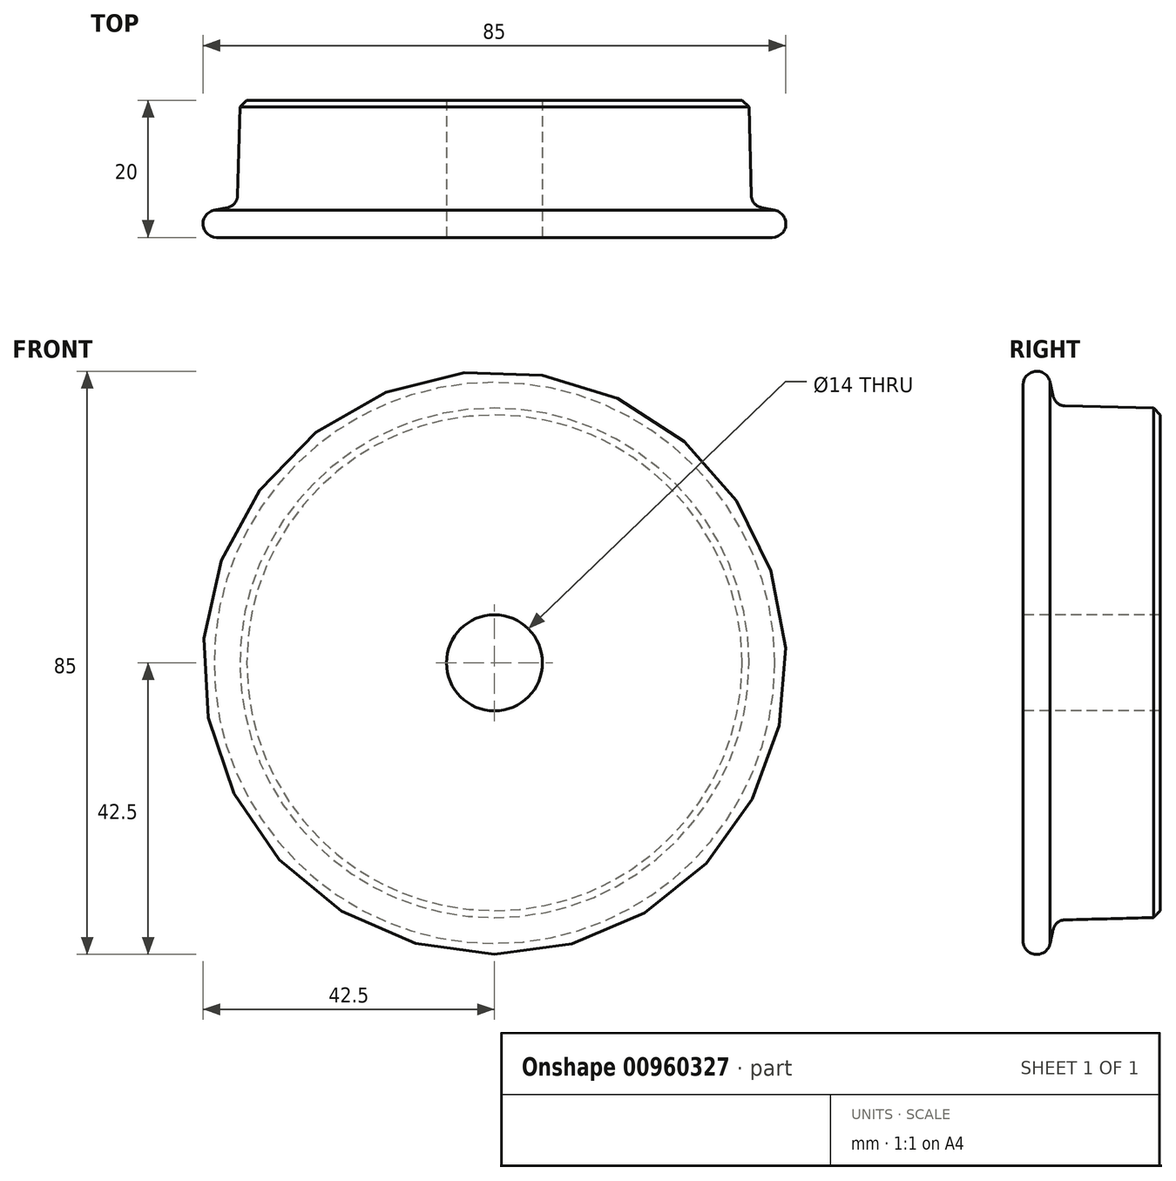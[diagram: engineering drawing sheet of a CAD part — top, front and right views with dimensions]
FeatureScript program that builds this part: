
annotation { "Feature Type Name" : "Feature", "Feature Type Description" : "" }
export const myFeature = defineFeature(function(context is Context, id is Id, definition is map)
    precondition{}
    {
        {
            var Q0;
            Q0=qCreatedBy(makeId("Right.planeOp"),FACE);
            var sketch = newSketch(context, id + "F0", { "sketchPlane" : qUnion([Q0])});
            skLineSegment(sketch, "E0", {"start": v(-29.18, 0) * mm, "end": v(26, 0) * mm, "construction": true});
            skLineSegment(sketch, "E1", {"start": v(0, 0) * mm, "end": v(0, 48.26) * mm, "construction": true});
            skLineSegment(sketch, "E2.0", {"start": v(-10, 7) * mm, "end": v(-10, 40.5) * mm});
            skArc(sketch, "E3", {"start": v(-6, 40.5) * mm, "mid": v(-8, 42.5) * mm, "end": v(-10, 40.5) * mm});
            skLineSegment(sketch, "E4", {"start": v(-6.04, 40.89) * mm, "end": v(-5.32, 37.5) * mm});
            skLineSegment(sketch, "E5.0", {"start": v(10, 7) * mm, "end": v(10, 37.1) * mm});
            skPoint(sketch, "E6.orphan", {"position": v(-10, 48.26) * mm});
            skLineSegment(sketch, "E7.0", {"start": v(-10, 7) * mm, "end": v(10, 7) * mm});
            skLineSegment(sketch, "E8", {"start": v(-5.32, 37.5) * mm, "end": v(10, 37.1) * mm});
            skSolve(sketch);
        }
        {
            var Q0;
            {var subQ2=sQuery(id+"F0.wireOp",EDGE,"E2.0");Q0=makeQuery(id+"F0.imprint","IMPRINT",FACE,{"disambiguationData":[TD([[makeQuery(id+"F0.imprint","IMPRINT",EDGE,{"derivedFrom":subQ2}),-1.0]])]});}
            var Q1;
            Q1=sQuery(id+"F0.wireOp",EDGE,"E0");
            revolve(context, id + "F1", {"surfaceOperationType" : NewSurfaceOperationType.NEW, "entities" : qUnion([Q0]), "axis" : qUnion([Q1]), "revolveType" : RevolveType.FULL});
        }
        {
            var Q0;
            Q0=makeQuery(id+"F1.opRevolve","SWEPT_EDGE",EDGE,{"disambiguationData":[OSD([sQuery(id+"F0.wireOp",EDGE,"E4"),sQuery(id+"F0.wireOp",EDGE,"E8")])]});
            fillet(context, id + "F2", {"entities" : qUnion([Q0]), "radius" : 1.8 * mm, "tangentPropagation" : true, "allowEdgeOverflow" : false});
        }
        {
            var Q0;
            Q0=makeQuery(id+"F1.opRevolve","SWEPT_EDGE",EDGE,{"disambiguationData":[OSD([sQuery(id+"F0.wireOp",EDGE,"E5.0"),sQuery(id+"F0.wireOp",EDGE,"E8")])]});
            chamfer(context, id + "F3", {"entities" : qUnion([Q0]), "width" : 1 * mm, "tangentPropagation" : true});
        }
    });
